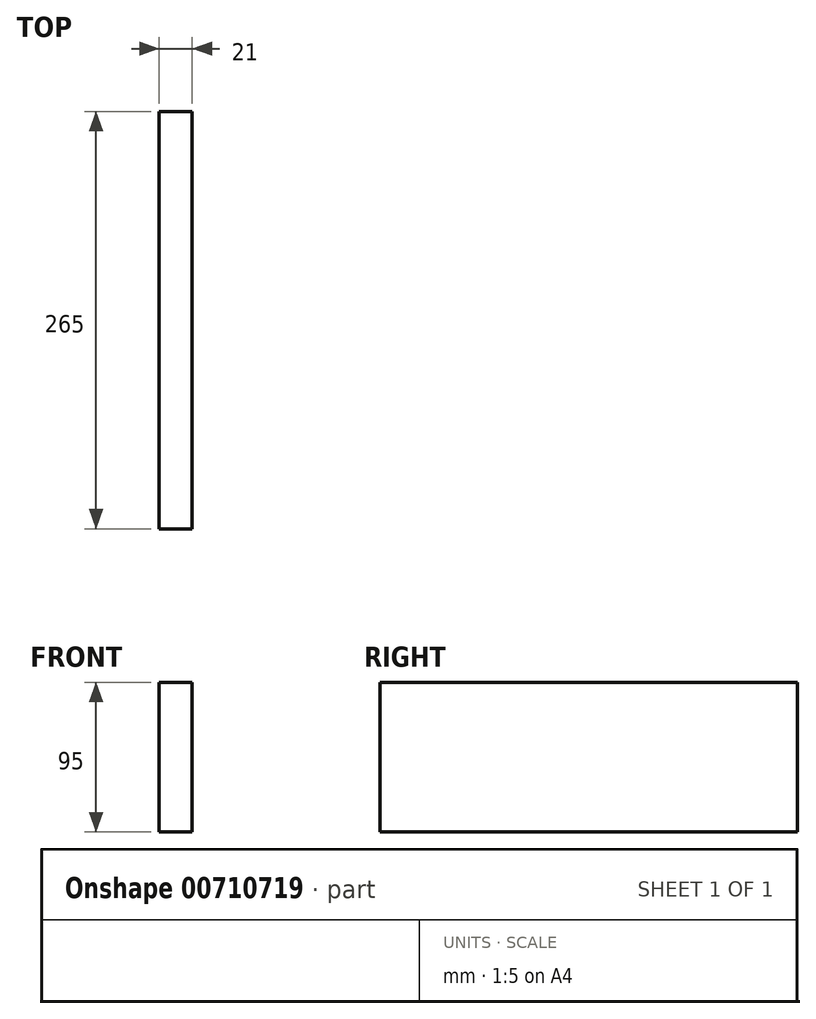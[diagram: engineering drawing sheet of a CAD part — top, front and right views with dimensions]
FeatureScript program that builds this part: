
annotation { "Feature Type Name" : "Feature", "Feature Type Description" : "" }
export const myFeature = defineFeature(function(context is Context, id is Id, definition is map)
    precondition{}
    {
        {
            assignVariable(context, id + "F0", {"name" : "l", "anyValue" : 265});
        }
        {
            var Q0;
            Q0=qCreatedBy(makeId("Front.planeOp"),FACE);
            var sketch = newSketch(context, id + "F1", { "sketchPlane" : qUnion([Q0])});
            skLineSegment(sketch, "E0.bottom", {"start": v(0, 0) * mm, "end": v(21, 0) * mm});
            skLineSegment(sketch, "E0.top", {"start": v(0, 95) * mm, "end": v(21, 95) * mm});
            skLineSegment(sketch, "E0.left", {"start": v(0, 0) * mm, "end": v(0, 95) * mm});
            skLineSegment(sketch, "E0.right", {"start": v(21, 0) * mm, "end": v(21, 95) * mm});
            skSolve(sketch);
        }
        {
            var Q0;
            Q0=qSketchRegion(id+"F1",true);
            extrude(context, id + "F2", {"entities" : qUnion([Q0]), "depth" : (getVariable(context, 'l')) * mm, "offsetDistance" : 25 * mm});
        }
    });
